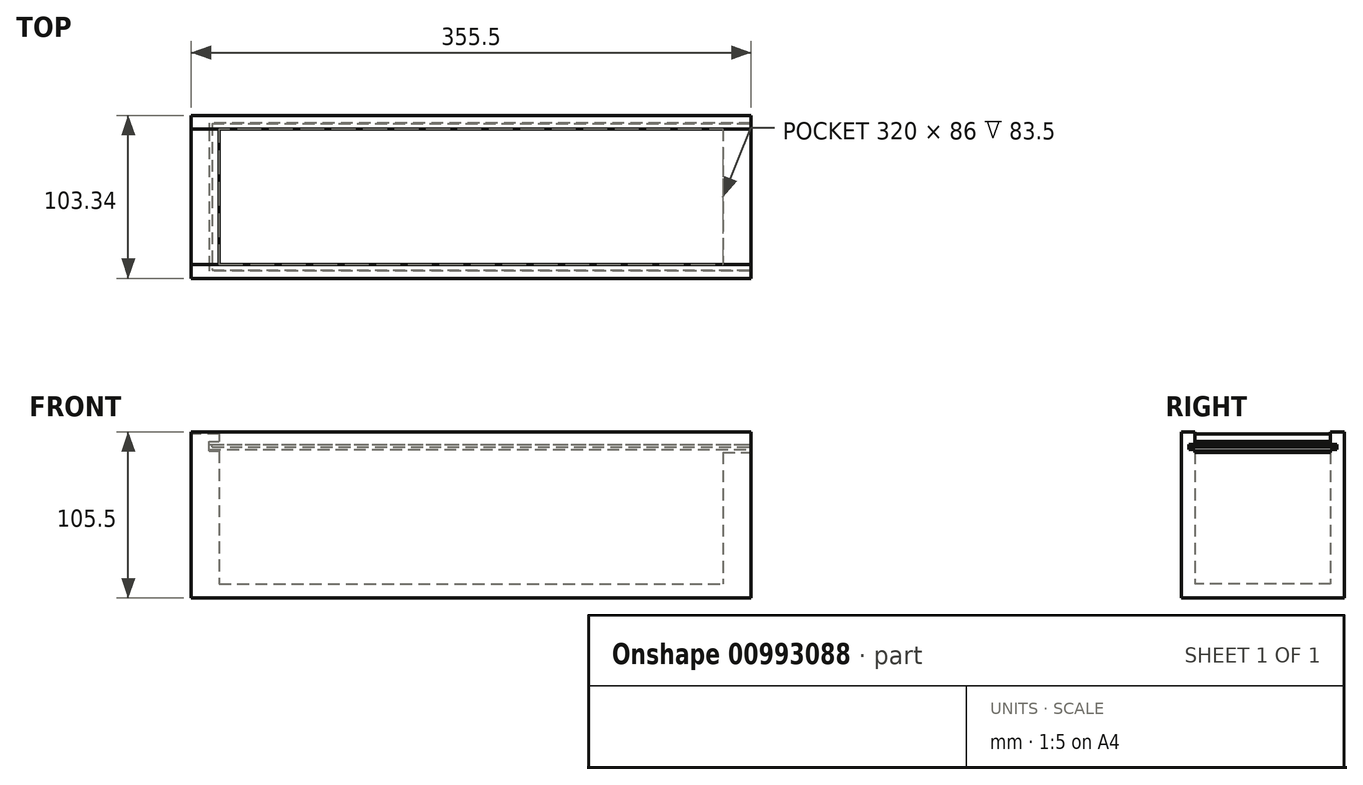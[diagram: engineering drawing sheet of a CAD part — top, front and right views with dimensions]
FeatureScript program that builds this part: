
annotation { "Feature Type Name" : "Feature", "Feature Type Description" : "" }
export const myFeature = defineFeature(function(context is Context, id is Id, definition is map)
    precondition{}
    {
        {
            var Q0;
            Q0=qCreatedBy(makeId("Top.planeOp"),FACE);
            var sketch = newSketch(context, id + "F0", { "sketchPlane" : qUnion([Q0])});
            skLineSegment(sketch, "E0.bottom", {"start": v(-177.75, 51.68) * mm, "end": v(177.75, 51.68) * mm});
            skLineSegment(sketch, "E0.top", {"start": v(-177.75, -51.67) * mm, "end": v(177.75, -51.67) * mm});
            skLineSegment(sketch, "E0.left", {"start": v(-177.75, 51.68) * mm, "end": v(-177.75, -51.67) * mm});
            skLineSegment(sketch, "E0.right", {"start": v(177.75, 51.68) * mm, "end": v(177.75, -51.67) * mm});
            skPoint(sketch, "E0.middle", {"position": v(0, 0) * mm});
            skLineSegment(sketch, "E1.bottom", {"start": v(-160, 43) * mm, "end": v(160, 43) * mm});
            skLineSegment(sketch, "E1.top", {"start": v(-160, -43) * mm, "end": v(160, -43) * mm});
            skLineSegment(sketch, "E1.left", {"start": v(-160, 43) * mm, "end": v(-160, -43) * mm});
            skLineSegment(sketch, "E1.right", {"start": v(160, 43) * mm, "end": v(160, -43) * mm});
            skPoint(sketch, "E2", {"position": v(0, 43) * mm});
            skPoint(sketch, "E3", {"position": v(-160, 0) * mm});
            skPoint(sketch, "E3.positionSnap0", {"position": v(-160, 0) * mm});
            skLineSegment(sketch, "E4", {"start": v(160, 43) * mm, "end": v(177.75, 43) * mm});
            skLineSegment(sketch, "E5", {"start": v(160, -43) * mm, "end": v(177.75, -43) * mm});
            skLineSegment(sketch, "E6", {"start": v(-160, -43) * mm, "end": v(-177.75, -43) * mm});
            skLineSegment(sketch, "E7", {"start": v(-160, 43) * mm, "end": v(-177.75, 43) * mm});
            skSolve(sketch);
        }
        {
            var Q0;
            Q0=makeQuery(id+"F0.imprint","IMPRINT",FACE,{"disambiguationData":[TD([[makeQuery(id+"F0.imprint","IMPRINT",EDGE,{"derivedFrom":sQuery(id+"F0.wireOp",EDGE,"E1.bottom")}),-1.0]])]});
            extrude(context, id + "F1", {"entities" : qUnion([Q0]), "depth" : 9 * mm, "offsetDistance" : 25 * mm});
        }
        {
            var Q0;
            Q0=makeQuery(id+"F0.imprint","IMPRINT",FACE,{"disambiguationData":[TD([[makeQuery(id+"F0.imprint","IMPRINT",EDGE,{"derivedFrom":sQuery(id+"F0.wireOp",EDGE,"E1.right")}),1.0]])]});
            extrude(context, id + "F2", {"entities" : qUnion([Q0]), "operationType" : NewBodyOperationType.ADD, "depth" : 92.5 * mm, "offsetDistance" : 25 * mm});
        }
        {
            var Q0;
            {var subQ1=sQuery(id+"F0.wireOp",EDGE,"E0.bottom");Q0=makeQuery(id+"F0.imprint","IMPRINT",FACE,{"disambiguationData":[TD([[makeQuery(id+"F0.imprint","IMPRINT",EDGE,{"derivedFrom":subQ1}),-1.0]])]});}
            var Q1;
            {var subQ1=sQuery(id+"F0.wireOp",EDGE,"E0.top");Q1=makeQuery(id+"F0.imprint","IMPRINT",FACE,{"disambiguationData":[TD([[makeQuery(id+"F0.imprint","IMPRINT",EDGE,{"derivedFrom":subQ1}),1.0]])]});}
            extrude(context, id + "F3", {"entities" : qUnion([Q0, Q1]), "operationType" : NewBodyOperationType.ADD, "depth" : 105.5 * mm, "offsetDistance" : 25 * mm});
        }
        {
            var Q0;
            Q0=makeQuery(id+"F0.imprint","IMPRINT",FACE,{"disambiguationData":[TD([[makeQuery(id+"F0.imprint","IMPRINT",EDGE,{"derivedFrom":sQuery(id+"F0.wireOp",EDGE,"E1.left")}),-1.0]])]});
            extrude(context, id + "F4", {"entities" : qUnion([Q0]), "operationType" : NewBodyOperationType.ADD, "depth" : 104 * mm, "offsetDistance" : 25 * mm});
        }
        {
            var Q0;
            Q0=makeQuery(id+"F3.opExtrude","CAP_FACE",FACE,{"disambiguationData":[OSD([sQuery(id+"F0.wireOp",EDGE,"E0.bottom"),sQuery(id+"F0.wireOp",EDGE,"E0.left"),sQuery(id+"F0.wireOp",EDGE,"E0.right"),sQuery(id+"F0.wireOp",EDGE,"E1.bottom"),sQuery(id+"F0.wireOp",EDGE,"E4"),sQuery(id+"F0.wireOp",EDGE,"E7")])],"isStart":false});
            cPlane(context, id + "F5", {"entities" : qUnion([Q0]), "cplaneType" : CPlaneType.OFFSET, "offset" : 8 * mm, "oppositeDirection" : true, "width" : 150 * mm, "height" : 150 * mm});
        }
        {
            var Q0;
            Q0=qCreatedBy(id+"F5.planeOp",FACE);
            var sketch = newSketch(context, id + "F6", { "sketchPlane" : qUnion([Q0])});
            skLineSegment(sketch, "E8", {"start": v(-160, 43) * mm, "end": v(177.75, 43) * mm, "construction": true});
            skLineSegment(sketch, "E9", {"start": v(-160, -43) * mm, "end": v(-160, 43) * mm, "construction": true});
            skLineSegment(sketch, "E10", {"start": v(177.75, -43) * mm, "end": v(-160, -43) * mm, "construction": true});
            skLineSegment(sketch, "E11.0", {"start": v(160, 43) * mm, "end": v(160, -43) * mm, "construction": true});
            skLineSegment(sketch, "E12", {"start": v(177.75, 47) * mm, "end": v(-166.5, 47) * mm});
            skLineSegment(sketch, "E13", {"start": v(160, 0) * mm, "end": v(-160, 0) * mm, "construction": true});
            skLineSegment(sketch, "E14.MirrorCS", {"start": v(177.75, -47) * mm, "end": v(-166.5, -47) * mm});
            skLineSegment(sketch, "E15", {"start": v(-166.5, 47) * mm, "end": v(-166.5, -47) * mm});
            skLineSegment(sketch, "E16.0", {"start": v(177.75, 51.68) * mm, "end": v(177.75, -51.67) * mm});
            skSolve(sketch);
        }
        {
            var Q0;
            {var subQ0=sQuery(id+"F6.wireOp",EDGE,"E12");Q0=makeQuery(id+"F6.imprint","IMPRINT",FACE,{"disambiguationData":[TD([[makeQuery(id+"F6.imprint","IMPRINT",EDGE,{"derivedFrom":subQ0}),1.0]])]});}
            extrude(context, id + "F7", {"entities" : qUnion([Q0]), "operationType" : NewBodyOperationType.REMOVE, "oppositeDirection" : true, "depth" : 3.3 * mm, "offsetDistance" : 25 * mm});
        }
        {
            var Q0;
            {var subQ0=sQuery(id+"F0.wireOp",EDGE,"E1.left");var subQ1=sQuery(id+"F0.wireOp",EDGE,"E1.top");var subQ2=sQuery(id+"F0.wireOp",EDGE,"E1.bottom");Q0=makeQuery(id+"F7.boolean.opBoolean","SPLIT",FACE,{"disambiguationData":[TD([makeQuery(id+"F1.opExtrude","CAP_FACE",FACE,{"disambiguationData":[OSD([subQ2,subQ1,subQ0,sQuery(id+"F0.wireOp",EDGE,"E1.right")])],"isStart":false})])],"derivedFrom":makeQuery(id+"F4.opExtrude","SWEPT_FACE",FACE,{"disambiguationData":[OSD([subQ0])]})});}
            var sketch = newSketch(context, id + "F8", { "sketchPlane" : qUnion([Q0])});
            skLineSegment(sketch, "E17.0", {"start": v(43, 94.2) * mm, "end": v(43, 9) * mm, "construction": true});
            skLineSegment(sketch, "E18.0", {"start": v(-43, 94.2) * mm, "end": v(-43, 9) * mm, "construction": true});
            skLineSegment(sketch, "E19.0", {"start": v(43, 94.2) * mm, "end": v(-43, 94.2) * mm, "construction": true});
            skLineSegment(sketch, "E20.0", {"start": v(43, 97.5) * mm, "end": v(-43, 97.5) * mm, "construction": true});
            skLineSegment(sketch, "E21.bottom", {"start": v(43, 93.3) * mm, "end": v(-43, 93.3) * mm});
            skLineSegment(sketch, "E21.top", {"start": v(43, 99.3) * mm, "end": v(-43, 99.3) * mm});
            skLineSegment(sketch, "E21.left", {"start": v(43, 93.3) * mm, "end": v(43, 99.3) * mm});
            skLineSegment(sketch, "E21.right", {"start": v(-43, 93.3) * mm, "end": v(-43, 99.3) * mm});
            skLineSegment(sketch, "E22.0", {"start": v(43, 104) * mm, "end": v(-43, 104) * mm, "construction": true});
            skSolve(sketch);
        }
        {
            var Q0;
            Q0 = qSketchRegion(id + "F8", true);
            extrude(context, id + "F9", {"entities" : qUnion([Q0]), "operationType" : NewBodyOperationType.REMOVE, "oppositeDirection" : true, "depth" : 6.5 * mm, "offsetDistance" : 25 * mm});
        }
        {
            var Q0;
            Q0=qCreatedBy(id+"F5.planeOp",FACE);
            var sketch = newSketch(context, id + "F10", { "sketchPlane" : qUnion([Q0])});
            skPoint(sketch, "E23.0", {"position": v(177.75, 0) * mm});
            skLineSegment(sketch, "E24.bottom", {"start": v(-164.55, 46.5) * mm, "end": v(177.75, 46.5) * mm});
            skLineSegment(sketch, "E24.top", {"start": v(-164.55, -46.5) * mm, "end": v(177.75, -46.5) * mm});
            skLineSegment(sketch, "E24.left", {"start": v(-164.55, 46.5) * mm, "end": v(-164.55, -46.5) * mm});
            skLineSegment(sketch, "E24.right", {"start": v(177.75, 46.5) * mm, "end": v(177.75, -46.5) * mm});
            skPoint(sketch, "E24.middle", {"position": v(6.6, 0) * mm});
            skSolve(sketch);
        }
        {
            var Q0;
            Q0=makeQuery(id+"F10.imprint","IMPRINT",FACE,{"disambiguationData":[TD([[makeQuery(id+"F10.imprint","IMPRINT",EDGE,{"derivedFrom":sQuery(id+"F10.wireOp",EDGE,"E24.bottom")}),-1.0]])]});
            extrude(context, id + "F11", {"entities" : qUnion([Q0]), "oppositeDirection" : true, "depth" : 1.5 * mm, "offsetDistance" : 25 * mm});
        }
    });
